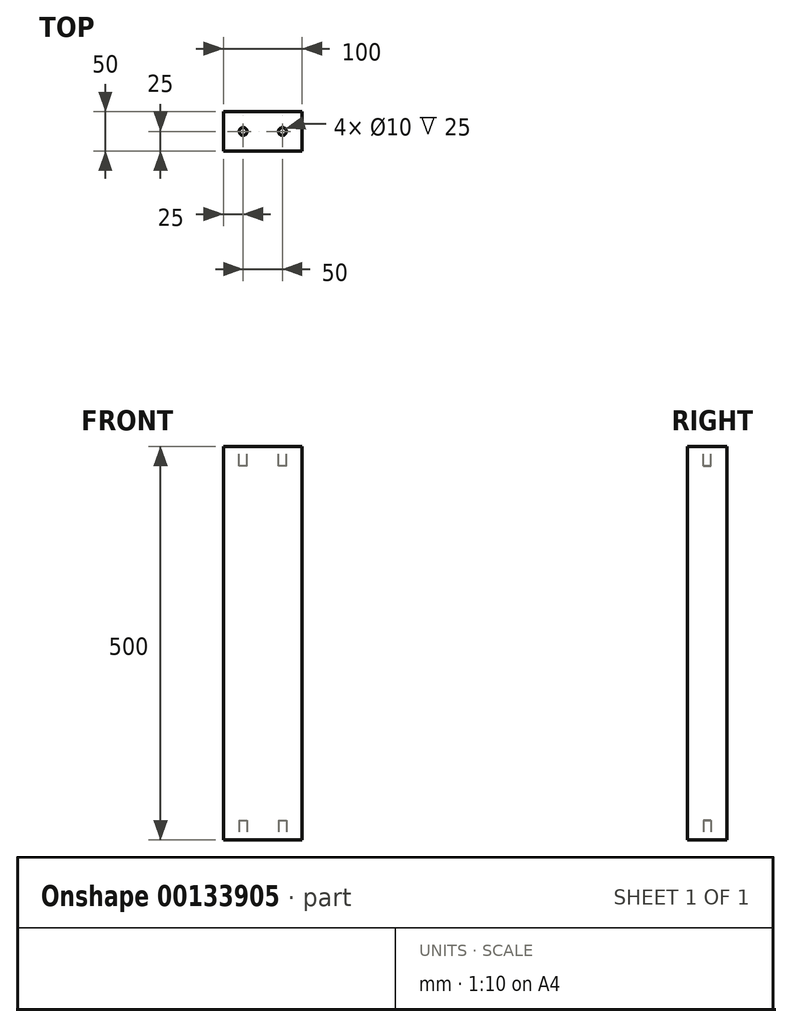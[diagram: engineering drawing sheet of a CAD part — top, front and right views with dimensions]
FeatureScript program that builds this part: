
annotation { "Feature Type Name" : "Feature", "Feature Type Description" : "" }
export const myFeature = defineFeature(function(context is Context, id is Id, definition is map)
    precondition{}
    {
        {
            var Q0;
            Q0=qCreatedBy(makeId("Front.planeOp"),FACE);
            var sketch = newSketch(context, id + "F0", { "sketchPlane" : qUnion([Q0])});
            skLineSegment(sketch, "E0.bottom", {"start": v(50, -250) * mm, "end": v(-50, -250) * mm});
            skLineSegment(sketch, "E0.top", {"start": v(50, 250) * mm, "end": v(-50, 250) * mm});
            skLineSegment(sketch, "E0.left", {"start": v(50, -250) * mm, "end": v(50, 250) * mm});
            skLineSegment(sketch, "E0.right", {"start": v(-50, -250) * mm, "end": v(-50, 250) * mm});
            skPoint(sketch, "E0.middle", {"position": v(0, 0) * mm});
            skSolve(sketch);
        }
        {
            var Q0;
            Q0=makeQuery(id+"F0.imprint","IMPRINT",FACE,{"disambiguationData":[TD([[makeQuery(id+"F0.imprint","IMPRINT",EDGE,{"derivedFrom":sQuery(id+"F0.wireOp",EDGE,"E0.bottom")}),-1.0]])]});
            extrude(context, id + "F1", {"entities" : qUnion([Q0]), "depth" : 50 * mm});
        }
        {
            var Q0;
            Q0=makeQuery(id+"F1.opExtrude","SWEPT_FACE",FACE,{"disambiguationData":[OSD([sQuery(id+"F0.wireOp",EDGE,"E0.top")])]});
            var sketch = newSketch(context, id + "F2", { "sketchPlane" : qUnion([Q0])});
            skCircle(sketch, "E1", {"center": v(-25, -25) * mm, "radius": 5 * mm});
            skPoint(sketch, "E1.centerSnap0", {"position": v(-50, -25) * mm});
            skCircle(sketch, "E2", {"center": v(25, -25) * mm, "radius": 5 * mm});
            skPoint(sketch, "E2.centerSnap0", {"position": v(50, -25) * mm});
            skSolve(sketch);
        }
        {
            var Q0;
            Q0=makeQuery(id+"F2.imprint","IMPRINT",FACE,{"disambiguationData":[TD([[makeQuery(id+"F2.imprint","IMPRINT",EDGE,{"derivedFrom":sQuery(id+"F2.wireOp",EDGE,"E1")}),1.0]])]});
            var Q1;
            Q1=makeQuery(id+"F2.imprint","IMPRINT",FACE,{"disambiguationData":[TD([[makeQuery(id+"F2.imprint","IMPRINT",EDGE,{"derivedFrom":sQuery(id+"F2.wireOp",EDGE,"E2")}),1.0]])]});
            extrude(context, id + "F3", {"entities" : qUnion([Q0, Q1]), "operationType" : NewBodyOperationType.REMOVE, "oppositeDirection" : true, "depth" : 25 * mm});
        }
        {
            var Q0;
            Q0=makeQuery(id+"F1.opExtrude","SWEPT_FACE",FACE,{"disambiguationData":[OSD([sQuery(id+"F0.wireOp",EDGE,"E0.bottom")])]});
            var sketch = newSketch(context, id + "F4", { "sketchPlane" : qUnion([Q0])});
            skCircle(sketch, "E3", {"center": v(25, 25) * mm, "radius": 5 * mm});
            skPoint(sketch, "E3.centerSnap0", {"position": v(50, 25) * mm});
            skCircle(sketch, "E4", {"center": v(-25, 25) * mm, "radius": 5 * mm});
            skPoint(sketch, "E4.centerSnap0", {"position": v(-50, 25) * mm});
            skSolve(sketch);
        }
        {
            var Q0;
            Q0=makeQuery(id+"F4.imprint","IMPRINT",FACE,{"disambiguationData":[TD([[makeQuery(id+"F4.imprint","IMPRINT",EDGE,{"derivedFrom":sQuery(id+"F4.wireOp",EDGE,"E3")}),1.0]])]});
            var Q1;
            Q1=makeQuery(id+"F4.imprint","IMPRINT",FACE,{"disambiguationData":[TD([[makeQuery(id+"F4.imprint","IMPRINT",EDGE,{"derivedFrom":sQuery(id+"F4.wireOp",EDGE,"E4")}),1.0]])]});
            extrude(context, id + "F5", {"entities" : qUnion([Q0, Q1]), "operationType" : NewBodyOperationType.REMOVE, "oppositeDirection" : true, "depth" : 25 * mm});
        }
    });
